# Revit family: Table-LAMMHULTS-FUNK-Circular
name_source: partatom
category: Furniture
revit_build: Autodesk Revit Architecture 2012 (Build: 20110916_2132(x64)
units: mm (PartAtom-declared; Revit-internal decimal feet)

## types (6) — shared parameters
Assembly Code = E2020
Description = *Please enter mtrl description here for use in mto*
Keynote = 46.B
Legs Material = Metal - White/Grey - Matte
Manufacturer = LAMMHULTS
Model = FUNK
Table Edge Material = Melamine - Stain - White/Grey
Table Top Material = Melamine - Stain - White/Grey
URL = www.lammhults.se

## per-type parameters (varying)
| type | Diameter | Leg Thickness | Leg Vault Height | Leg Width | Table Top Height | Table Top Length | Table Top Width |
| H45 D100 Laminate WhiteGrey | 1000 mm  [stored 3.28084 ft] | 35 mm  [stored 0.114829 ft] | 114 mm  [stored 0.374016 ft] | 670 mm  [stored 2.19816 ft] | 450 mm  [stored 1.47638 ft] | 1000 mm  [stored 3.28084 ft] | 1000 mm  [stored 3.28084 ft] |
| H72 D70  Laminate WhiteGrey | 700 mm | 35 mm  [stored 0.114829 ft] | 114 mm  [stored 0.374016 ft] | 670 mm  [stored 2.19816 ft] | 720 mm | 700 mm | 700 mm |
| H72 D100  Laminate WhiteGrey | 1000 mm  [stored 3.28084 ft] | 35 mm  [stored 0.114829 ft] | 114 mm  [stored 0.374016 ft] | 670 mm  [stored 2.19816 ft] | 720 mm | 1000 mm  [stored 3.28084 ft] | 1000 mm  [stored 3.28084 ft] |
| H72 D120  Laminate WhiteGrey | 1200 mm | 44 mm | 147 mm | 868 mm | 720 mm | 1200 mm | 1200 mm |
| H72 D140  Laminate WhiteGrey | 1400 mm | 44 mm | 147 mm | 868 mm | 720 mm | 1400 mm | 1400 mm |
| H110 D70  Laminate WhiteGrey | 700 mm | 35 mm  [stored 0.114829 ft] | 114 mm  [stored 0.374016 ft] | 670 mm  [stored 2.19816 ft] | 1100 mm | 700 mm | 700 mm |

note: [stored X ft] marks values corroborated as IEEE doubles in the binary element streams (Revit-internal decimal feet)

## geometry (parser evidence)
native form markers: Blend x5, Sweep x1
no freeform markers — native parametric forms only
